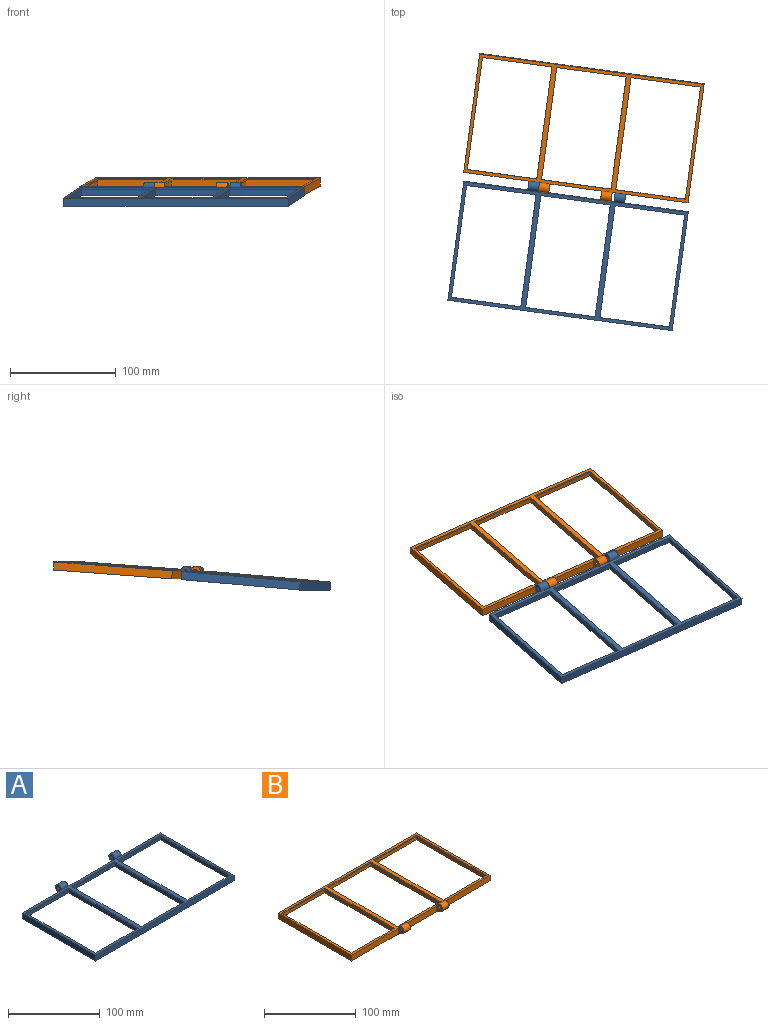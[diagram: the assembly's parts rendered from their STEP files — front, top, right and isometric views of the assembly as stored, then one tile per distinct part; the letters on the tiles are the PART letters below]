
ASSEMBLY  parts=2 mates=1
PART A: 45 faces, bbox 214.1x122.3x12.1 mm
  f0: plane 60.9x7.6mm, normal (0,1,0), area 462.8mm2, adj f3,f18,f33,f43
  f1: plane 72.3x7.6mm, normal (0,1,0), area 549.5mm2, adj f18,f33,f39,f44
  f2: plane 60.9x7.6mm, normal (0,1,0), area 462.8mm2, adj f17,f18,f33,f38
  f3: plane 113.3x7.6mm, normal (-1,0,0), area 861.1mm2, adj f0,f4,f18,f33
  f4: plane 214.1x7.6mm, normal (0,-1,0), area 1627.2mm2, adj f3,f17,f18,f33
  f5: plane 110.5x6mm, normal (1,0,0), area 663mm2, adj f6,f14,f18,f34
  f6: plane 69.5x6mm, normal (0,-1,0), area 417mm2, adj f5,f7,f18,f34
  f7: plane 110.5x6mm, normal (-1,0,0), area 663mm2, adj f6,f14,f18,f34
  f8: plane 110.5x6mm, normal (1,0,0), area 663mm2, adj f9,f15,f18,f20
  f9: plane 69.5x6mm, normal (0,-1,0), area 417mm2, adj f8,f10,f18,f20
  f10: plane 110.5x6mm, normal (-1,0,0), area 663mm2, adj f9,f15,f18,f20
  f11: plane 110.5x6mm, normal (1,0,0), area 663mm2, adj f12,f16,f18,f19
  f12: plane 69.5x6mm, normal (0,-1,0), area 417mm2, adj f11,f13,f18,f19
  f13: plane 110.5x6mm, normal (-1,0,0), area 663mm2, adj f12,f16,f18,f19
  f14: plane 69.5x6mm, normal (0,1,0), area 417mm2, adj f5,f7,f18,f34
  f15: plane 69.5x6mm, normal (0,1,0), area 417mm2, adj f8,f10,f18,f20
  f16: plane 69.5x6mm, normal (0,1,0), area 417mm2, adj f11,f13,f18,f19
  f17: plane 113.3x7.6mm, normal (1,0,0), area 861.1mm2, adj f2,f4,f18,f33
  f18: plane 214.1x113.3mm, normal (0,0,-1), area 1218.3mm2, adj f0,f1,f2,f3,f4,f5,f6,f7
  f19: plane 110.5x69.5mm, normal (0,0,-1), area 565.8mm2, adj f11,f12,f13,f16,f21,f22,f23,f32
  f20: plane 110.5x69.5mm, normal (0,0,-1), area 565.8mm2, adj f8,f9,f10,f15,f24,f25,f26,f30
  f21: plane 107.3x1.6mm, normal (1,0,0), area 171.7mm2, adj f19,f22,f32,f33
  f22: plane 66.3x1.6mm, normal (0,-1,0), area 106.1mm2, adj f19,f21,f23,f33
  f23: plane 107.3x1.6mm, normal (-1,0,0), area 171.7mm2, adj f19,f22,f32,f33
  f24: plane 107.3x1.6mm, normal (1,0,0), area 171.7mm2, adj f20,f25,f30,f33
  f25: plane 66.3x1.6mm, normal (0,-1,0), area 106.1mm2, adj f20,f24,f26,f33
  f26: plane 107.3x1.6mm, normal (-1,0,0), area 171.7mm2, adj f20,f25,f30,f33
  f27: plane 107.3x1.6mm, normal (1,0,0), area 171.7mm2, adj f28,f31,f33,f34
  f28: plane 66.3x1.6mm, normal (0,-1,0), area 106.1mm2, adj f27,f29,f33,f34
  f29: plane 107.3x1.6mm, normal (-1,0,0), area 171.7mm2, adj f28,f31,f33,f34
  f30: plane 66.3x1.6mm, normal (0,1,0), area 106.1mm2, adj f20,f24,f26,f33
  f31: plane 66.3x1.6mm, normal (0,1,0), area 106.1mm2, adj f27,f29,f33,f34
  f32: plane 66.3x1.6mm, normal (0,1,0), area 106.1mm2, adj f19,f21,f23,f33
  f33: plane 214.1x113.3mm, normal (0,0,1), area 2915.6mm2, adj f0,f1,f2,f3,f4,f17,f21,f22
  f34: plane 110.5x69.5mm, normal (0,0,-1), area 565.8mm2, adj f5,f6,f7,f14,f27,f28,f29,f31
  f35: cylinder r=4.5mm len=10mm, axis (-1,0,0), area 189.5mm2, adj f33,f37,f38,f39
  f36: cylinder r=1.55mm len=10mm, axis (-1,0,0), area 97.4mm2, adj f38,f39
  f37: plane 10x6.66mm, normal (0,0.48,-0.88), area 76mm2, adj f18,f35,f38,f39
  f38: plane 12.1x9mm, normal (1,0,0), area 69.3mm2, adj f2,f35,f36,f37
  f39: plane 12.1x9mm, normal (-1,0,0), area 69.3mm2, adj f1,f35,f36,f37
  f40: cylinder r=4.5mm len=10mm, axis (1,0,0), area 189.5mm2, adj f33,f41,f43,f44
  f41: plane 10x6.66mm, normal (0,0.48,-0.88), area 76mm2, adj f18,f40,f43,f44
  f42: cylinder r=1.55mm len=10mm, axis (1,0,0), area 97.4mm2, adj f43,f44
  f43: plane 12.1x9mm, normal (-1,0,0), area 69.3mm2, adj f0,f40,f41,f42
  f44: plane 12.1x9mm, normal (1,0,0), area 69.3mm2, adj f1,f40,f41,f42
PART B: 45 faces, bbox 214.1x122.3x12.1 mm
  f0: plane 49.5x7.6mm, normal (0,-1,0), area 376.2mm2, adj f18,f34,f38,f43
  f1: plane 72.3x7.6mm, normal (0,-1,0), area 549.5mm2, adj f3,f18,f34,f39
  f2: plane 72.3x7.6mm, normal (0,-1,0), area 549.5mm2, adj f17,f18,f34,f44
  f3: plane 113.3x7.6mm, normal (-1,0,0), area 861.1mm2, adj f1,f4,f18,f34
  f4: plane 214.1x7.6mm, normal (0,1,0), area 1627.2mm2, adj f3,f17,f18,f34
  f5: plane 110.5x6mm, normal (1,0,0), area 663mm2, adj f6,f14,f18,f21
  f6: plane 69.5x6mm, normal (0,1,0), area 417mm2, adj f5,f7,f18,f21
  f7: plane 110.5x6mm, normal (-1,0,0), area 663mm2, adj f6,f14,f18,f21
  f8: plane 110.5x6mm, normal (1,0,0), area 663mm2, adj f9,f15,f18,f20
  f9: plane 69.5x6mm, normal (0,1,0), area 417mm2, adj f8,f10,f18,f20
  f10: plane 110.5x6mm, normal (-1,0,0), area 663mm2, adj f9,f15,f18,f20
  f11: plane 110.5x6mm, normal (1,0,0), area 663mm2, adj f12,f16,f18,f19
  f12: plane 69.5x6mm, normal (0,1,0), area 417mm2, adj f11,f13,f18,f19
  f13: plane 110.5x6mm, normal (-1,0,0), area 663mm2, adj f12,f16,f18,f19
  f14: plane 69.5x6mm, normal (0,-1,0), area 417mm2, adj f5,f7,f18,f21
  f15: plane 69.5x6mm, normal (0,-1,0), area 417mm2, adj f8,f10,f18,f20
  f16: plane 69.5x6mm, normal (0,-1,0), area 417mm2, adj f11,f13,f18,f19
  f17: plane 113.3x7.6mm, normal (1,0,0), area 861.1mm2, adj f2,f4,f18,f34
  f18: plane 214.1x113.3mm, normal (0,0,-1), area 1218.3mm2, adj f0,f1,f2,f3,f4,f5,f6,f7
  f19: plane 110.5x69.5mm, normal (0,0,-1), area 565.8mm2, adj f11,f12,f13,f16,f28,f29,f30,f32
  f20: plane 110.5x69.5mm, normal (0,0,-1), area 565.8mm2, adj f8,f9,f10,f15,f25,f26,f27,f31
  f21: plane 110.5x69.5mm, normal (0,0,-1), area 565.8mm2, adj f5,f6,f7,f14,f22,f23,f24,f33
  f22: plane 107.3x1.6mm, normal (1,0,0), area 171.7mm2, adj f21,f23,f33,f34
  f23: plane 66.3x1.6mm, normal (0,-1,0), area 106.1mm2, adj f21,f22,f24,f34
  f24: plane 107.3x1.6mm, normal (-1,0,0), area 171.7mm2, adj f21,f23,f33,f34
  f25: plane 107.3x1.6mm, normal (1,0,0), area 171.7mm2, adj f20,f26,f31,f34
  f26: plane 66.3x1.6mm, normal (0,-1,0), area 106.1mm2, adj f20,f25,f27,f34
  f27: plane 107.3x1.6mm, normal (-1,0,0), area 171.7mm2, adj f20,f26,f31,f34
  f28: plane 107.3x1.6mm, normal (1,0,0), area 171.7mm2, adj f19,f29,f32,f34
  f29: plane 66.3x1.6mm, normal (0,-1,0), area 106.1mm2, adj f19,f28,f30,f34
  f30: plane 107.3x1.6mm, normal (-1,0,0), area 171.7mm2, adj f19,f29,f32,f34
  f31: plane 66.3x1.6mm, normal (0,1,0), area 106.1mm2, adj f20,f25,f27,f34
  f32: plane 66.3x1.6mm, normal (0,1,0), area 106.1mm2, adj f19,f28,f30,f34
  f33: plane 66.3x1.6mm, normal (0,1,0), area 106.1mm2, adj f21,f22,f24,f34
  f34: plane 214.1x113.3mm, normal (0,0,1), area 2915.6mm2, adj f0,f1,f2,f3,f4,f17,f22,f23
  f35: cylinder r=4.5mm len=10mm, axis (-1,0,0), area 189.5mm2, adj f34,f36,f38,f39
  f36: plane 10x6.66mm, normal (0,-0.48,-0.88), area 76mm2, adj f18,f35,f38,f39
  f37: cylinder r=1.5mm len=10mm, axis (-1,0,0), area 94.2mm2, adj f38,f39
  f38: plane 12.1x9mm, normal (1,0,0), area 69.8mm2, adj f0,f35,f36,f37
  f39: plane 12.1x9mm, normal (-1,0,0), area 69.8mm2, adj f1,f35,f36,f37
  f40: cylinder r=4.5mm len=10mm, axis (1,0,0), area 189.5mm2, adj f34,f42,f43,f44
  f41: cylinder r=1.55mm len=10mm, axis (1,0,0), area 97.4mm2, adj f43,f44
  f42: plane 10x6.66mm, normal (0,-0.48,-0.88), area 76mm2, adj f18,f40,f43,f44
  f43: plane 12.1x9mm, normal (-1,0,0), area 69.3mm2, adj f0,f40,f41,f42
  f44: plane 12.1x9mm, normal (1,0,0), area 69.3mm2, adj f2,f40,f41,f42
PLACE A rot(axis=(0.54,-0.04,-0.84),9.2deg) t=(-12.28,-88.61,78.24)mm
PLACE B rot(axis=(0.48,-0.03,-0.88),8.8deg) t=(-16.15,-106.56,77.74)mm
MATE revolute A.f40 <-> B.f35  axis (0.99,-0.13,0) through (-23.78,-25.15,91.24)mm
